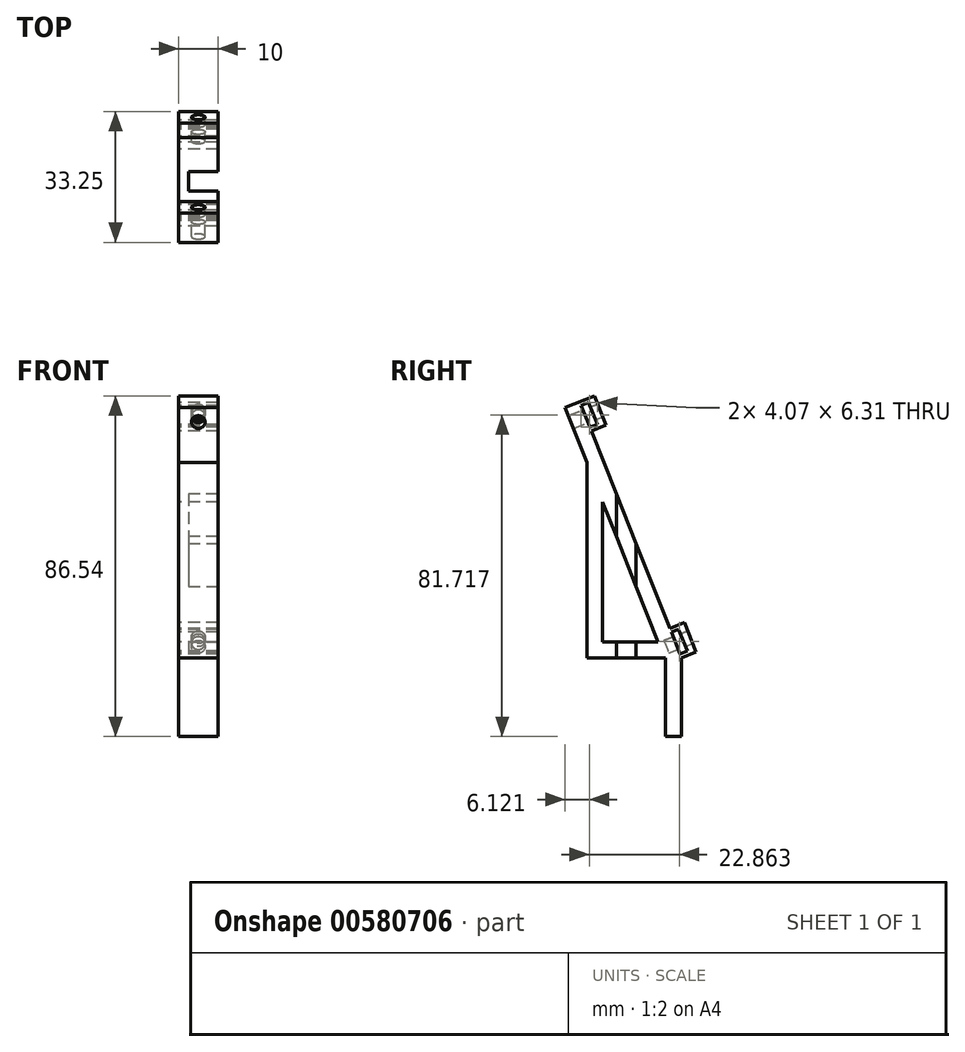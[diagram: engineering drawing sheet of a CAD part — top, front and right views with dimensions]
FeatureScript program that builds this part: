
annotation { "Feature Type Name" : "Feature", "Feature Type Description" : "" }
export const myFeature = defineFeature(function(context is Context, id is Id, definition is map)
    precondition{}
    {
        {
            var Q0;
            Q0=qCreatedBy(makeId("Right.planeOp"),FACE);
            var sketch = newSketch(context, id + "F0", { "sketchPlane" : qUnion([Q0])});
            skLineSegment(sketch, "E0", {"start": v(-20, 0) * mm, "end": v(0, 0) * mm});
            skLineSegment(sketch, "E1", {"start": v(0, 0) * mm, "end": v(0, -20) * mm});
            skLineSegment(sketch, "E2", {"start": v(0, -20) * mm, "end": v(4, -20) * mm});
            skLineSegment(sketch, "E3", {"start": v(4, -20) * mm, "end": v(4, 0) * mm});
            skLineSegment(sketch, "E4", {"start": v(4, 0) * mm, "end": v(-21.81, 65.07) * mm});
            skLineSegment(sketch, "E5", {"start": v(-21.81, 65.07) * mm, "end": v(-25.53, 63.6) * mm});
            skLineSegment(sketch, "E6", {"start": v(-25.53, 63.6) * mm, "end": v(-20, 49.65) * mm});
            skLineSegment(sketch, "E7", {"start": v(-20, 49.65) * mm, "end": v(-20, 0) * mm});
            skLineSegment(sketch, "E8", {"start": v(-16, 39.57) * mm, "end": v(-16, 4) * mm});
            skLineSegment(sketch, "E9", {"start": v(-16, 4) * mm, "end": v(-1.9, 4) * mm});
            skLineSegment(sketch, "E10", {"start": v(-1.9, 4) * mm, "end": v(-16, 39.57) * mm});
            skLineSegment(sketch, "E11", {"start": v(-21.81, 65.07) * mm, "end": v(-18.1, 66.54) * mm});
            skLineSegment(sketch, "E12", {"start": v(-18.1, 66.54) * mm, "end": v(-15.15, 59.1) * mm});
            skLineSegment(sketch, "E13", {"start": v(-15.15, 59.1) * mm, "end": v(-18.86, 57.63) * mm});
            skLineSegment(sketch, "E14", {"start": v(4, 0) * mm, "end": v(7.72, 1.48) * mm});
            skLineSegment(sketch, "E15", {"start": v(7.72, 1.48) * mm, "end": v(4.77, 8.91) * mm});
            skLineSegment(sketch, "E16", {"start": v(4.77, 8.91) * mm, "end": v(1.05, 7.44) * mm});
            skLineSegment(sketch, "E17", {"start": v(-21.44, 64.14) * mm, "end": v(-19.59, 64.87) * mm});
            skLineSegment(sketch, "E18", {"start": v(-19.59, 64.87) * mm, "end": v(-17.37, 59.3) * mm});
            skLineSegment(sketch, "E19", {"start": v(-17.37, 59.3) * mm, "end": v(-19.23, 58.56) * mm});
            skLineSegment(sketch, "E20", {"start": v(1.42, 6.5) * mm, "end": v(3.28, 7.24) * mm});
            skLineSegment(sketch, "E21", {"start": v(3.28, 7.24) * mm, "end": v(5.5, 1.67) * mm});
            skLineSegment(sketch, "E22", {"start": v(5.5, 1.67) * mm, "end": v(3.63, 0.93) * mm});
            skSolve(sketch);
        }
        {
            var Q0;
            Q0 = qSketchRegion(id + "F0", true);
            extrude(context, id + "F1", {"entities" : qUnion([Q0]), "depth" : 10 * mm, "offsetDistance" : 25 * mm});
        }
        {
            var Q0;
            Q0=makeQuery(id+"F1.opExtrude","SWEPT_FACE",FACE,{"disambiguationData":[OSD([sQuery(id+"F0.wireOp",EDGE,"E12")])]});
            var sketch = newSketch(context, id + "F2", { "sketchPlane" : qUnion([Q0])});
            skLineSegment(sketch, "E23", {"start": v(0, 60.52) * mm, "end": v(-10, 68.52) * mm, "construction": true});
            skCircle(sketch, "E24", {"center": v(-5, 64.52) * mm, "radius": 1.75 * mm});
            skSolve(sketch);
        }
        {
            var Q0;
            Q0 = qSketchRegion(id + "F2", true);
            extrude(context, id + "F3", {"entities" : qUnion([Q0]), "operationType" : NewBodyOperationType.REMOVE, "oppositeDirection" : true, "depth" : 25 * mm, "offsetDistance" : 25 * mm});
        }
        {
            var Q0;
            Q0=makeQuery(id+"F1.opExtrude","SWEPT_FACE",FACE,{"disambiguationData":[OSD([sQuery(id+"F0.wireOp",EDGE,"E15")])]});
            var sketch = newSketch(context, id + "F4", { "sketchPlane" : qUnion([Q0])});
            skLineSegment(sketch, "E25", {"start": v(0, -1.48) * mm, "end": v(-10, 6.52) * mm, "construction": true});
            skCircle(sketch, "E26", {"center": v(-5, 2.52) * mm, "radius": 1.75 * mm});
            skSolve(sketch);
        }
        {
            var Q0;
            Q0 = qSketchRegion(id + "F4", true);
            extrude(context, id + "F5", {"entities" : qUnion([Q0]), "operationType" : NewBodyOperationType.REMOVE, "oppositeDirection" : true, "depth" : 6.5 * mm, "offsetDistance" : 25 * mm});
        }
        {
            var Q0;
            Q0=makeQuery(id+"F1.opExtrude","SWEPT_FACE",FACE,{"disambiguationData":[OSD([sQuery(id+"F0.wireOp",EDGE,"E0")])]});
            var sketch = newSketch(context, id + "F6", { "sketchPlane" : qUnion([Q0])});
            skLineSegment(sketch, "E27", {"start": v(10, 12.5) * mm, "end": v(2.5, 12.5) * mm});
            skLineSegment(sketch, "E28", {"start": v(2.5, 12.5) * mm, "end": v(2.5, 7.5) * mm});
            skLineSegment(sketch, "E29", {"start": v(2.5, 7.5) * mm, "end": v(10, 7.5) * mm});
            skSolve(sketch);
        }
        {
            var Q0;
            Q0 = qSketchRegion(id + "F6", true);
            var Q1;
            {var subQ0=sQuery(id+"F6.wireOp",EDGE,"E27");Q1=makeQuery(id+"F6.imprint","IMPRINT",FACE,{"disambiguationData":[TD([[makeQuery(id+"F6.imprint","IMPRINT",EDGE,{"derivedFrom":subQ0}),1.0]])]});}
            extrude(context, id + "F7", {"entities" : qUnion([Q0, Q1]), "operationType" : NewBodyOperationType.REMOVE, "oppositeDirection" : true, "depth" : 52.6 * mm, "offsetDistance" : 25 * mm});
        }
    });
